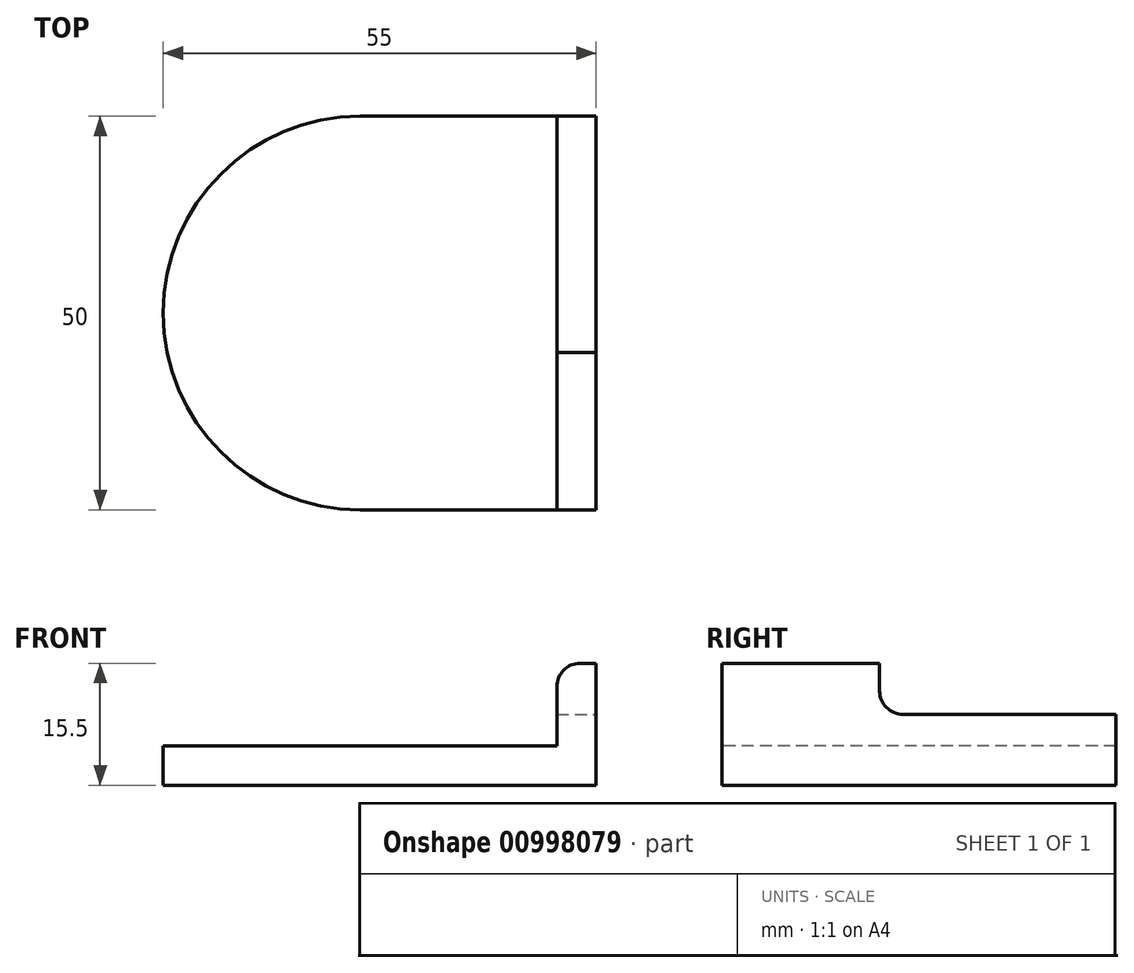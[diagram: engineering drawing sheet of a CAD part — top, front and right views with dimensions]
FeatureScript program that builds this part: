
annotation { "Feature Type Name" : "Feature", "Feature Type Description" : "" }
export const myFeature = defineFeature(function(context is Context, id is Id, definition is map)
    precondition{}
    {
        {
            var Q0;
            Q0=qCreatedBy(makeId("Top.planeOp"),FACE);
            var sketch = newSketch(context, id + "F0", { "sketchPlane" : qUnion([Q0])});
            skArc(sketch, "E0", {"start": v(0, 25) * mm, "mid": v(-25, 0) * mm, "end": v(0, -25) * mm});
            skLineSegment(sketch, "E1", {"start": v(0, 25) * mm, "end": v(30, 25) * mm});
            skLineSegment(sketch, "E2", {"start": v(30, -25) * mm, "end": v(0, -25) * mm});
            skLineSegment(sketch, "E3.trimOffspring", {"start": v(30, 25) * mm, "end": v(30, -25) * mm});
            skLineSegment(sketch, "E4", {"start": v(25, 36.59) * mm, "end": v(25, -50.52) * mm, "construction": true});
            skSolve(sketch);
        }
        {
            var Q0;
            Q0=qSketchRegion(id+"F0",true);
            extrude(context, id + "F1", {"entities" : qUnion([Q0]), "depth" : 5 * mm, "offsetDistance" : 25 * mm});
        }
        {
            var Q0;
            Q0=makeQuery(id+"F1.opExtrude","CAP_FACE",FACE,{"disambiguationData":[OSD([sQuery(id+"F0.wireOp",EDGE,"E0"),sQuery(id+"F0.wireOp",EDGE,"E1"),sQuery(id+"F0.wireOp",EDGE,"E2"),sQuery(id+"F0.wireOp",EDGE,"E3.trimOffspring")])],"isStart":false});
            var sketch = newSketch(context, id + "F2", { "sketchPlane" : qUnion([Q0])});
            skLineSegment(sketch, "E5.bottom", {"start": v(30, 25) * mm, "end": v(25, 25) * mm});
            skLineSegment(sketch, "E5.top", {"start": v(30, -25) * mm, "end": v(25, -25) * mm});
            skLineSegment(sketch, "E5.left", {"start": v(30, 25) * mm, "end": v(30, -25) * mm});
            skLineSegment(sketch, "E5.right", {"start": v(25, 25) * mm, "end": v(25, -25) * mm});
            skSolve(sketch);
        }
        {
            var Q0;
            Q0 = qSketchRegion(id + "F2", true);
            extrude(context, id + "F3", {"entities" : qUnion([Q0]), "operationType" : NewBodyOperationType.ADD, "depth" : 4 * mm, "offsetDistance" : 25 * mm});
        }
        {
            var Q0;
            Q0=makeQuery(id+"F1.opExtrude","CAP_FACE",FACE,{"disambiguationData":[OSD([sQuery(id+"F0.wireOp",EDGE,"E0"),sQuery(id+"F0.wireOp",EDGE,"E1"),sQuery(id+"F0.wireOp",EDGE,"E2"),sQuery(id+"F0.wireOp",EDGE,"E3.trimOffspring")])],"isStart":false});
            var sketch = newSketch(context, id + "F4", { "sketchPlane" : qUnion([Q0])});
            skLineSegment(sketch, "E6.bottom", {"start": v(30, -25) * mm, "end": v(25, -25) * mm});
            skLineSegment(sketch, "E6.top", {"start": v(30, -5) * mm, "end": v(25, -5) * mm});
            skLineSegment(sketch, "E6.left", {"start": v(30, -25) * mm, "end": v(30, -5) * mm});
            skLineSegment(sketch, "E6.right", {"start": v(25, -25) * mm, "end": v(25, -5) * mm});
            skSolve(sketch);
        }
        {
            var Q0;
            Q0 = qSketchRegion(id + "F4", true);
            extrude(context, id + "F5", {"entities" : qUnion([Q0]), "operationType" : NewBodyOperationType.ADD, "depth" : 10.5 * mm, "offsetDistance" : 25 * mm});
        }
        {
            var Q0;
            Q0=makeQuery(id+"F5.boolean.opBoolean","INTERSECT",EDGE,{"derivedFrom":[makeQuery(id+"F3.opExtrude","CAP_FACE",FACE,{"disambiguationData":[OSD([sQuery(id+"F2.wireOp",EDGE,"E5.bottom"),sQuery(id+"F2.wireOp",EDGE,"E5.top"),sQuery(id+"F2.wireOp",EDGE,"E5.left"),sQuery(id+"F2.wireOp",EDGE,"E5.right")])],"isStart":false}),makeQuery(id+"F5.opExtrude","SWEPT_FACE",FACE,{"disambiguationData":[OSD([sQuery(id+"F4.wireOp",EDGE,"E6.top")])]})]});
            var Q1;
            Q1=makeQuery(id+"F5.opExtrude","CAP_EDGE",EDGE,{"disambiguationData":[OSD([sQuery(id+"F4.wireOp",EDGE,"E6.right")])],"isStart":false});
            fillet(context, id + "F6", {"entities" : qUnion([Q0, Q1]), "radius" : 3 * mm, "tangentPropagation" : true, "allowEdgeOverflow" : false});
        }
    });
